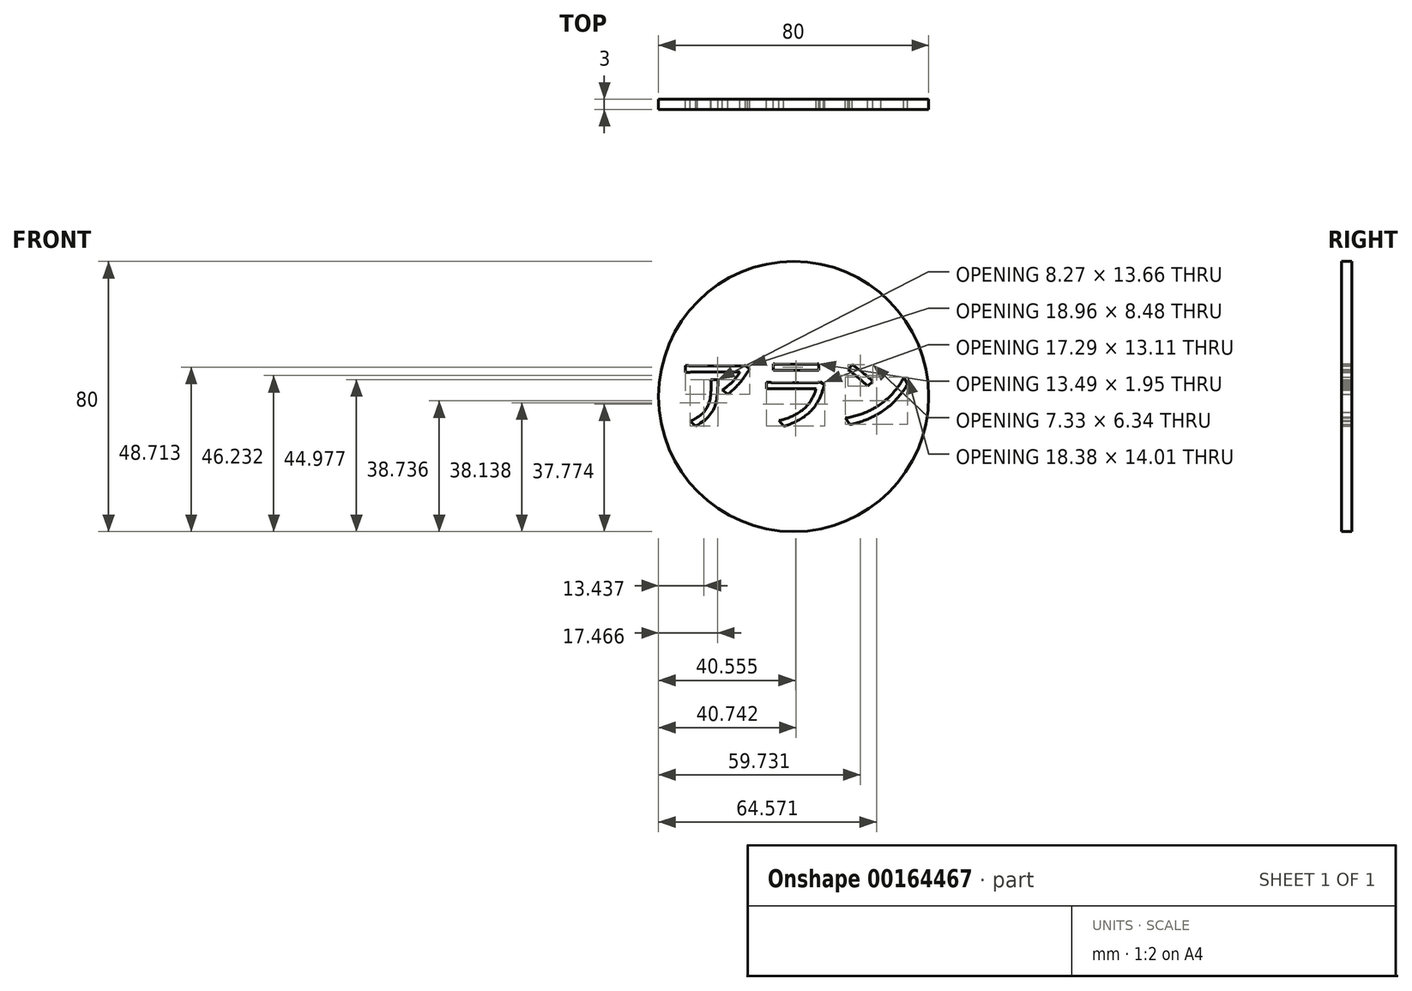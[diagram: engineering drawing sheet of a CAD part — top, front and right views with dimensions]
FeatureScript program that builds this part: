
annotation { "Feature Type Name" : "Feature", "Feature Type Description" : "" }
export const myFeature = defineFeature(function(context is Context, id is Id, definition is map)
    precondition{}
    {
        {
            var Q0;
            Q0=qCreatedBy(makeId("Front.planeOp"),FACE);
            var sketch = newSketch(context, id + "F0", { "sketchPlane" : qUnion([Q0])});
            skCircle(sketch, "E0", {"center": v(0, 0) * mm, "radius": 40 * mm});
            skText(sketch, "E1", { "text": "アラン", "fontName": "NotoSansCJKjp-Regular.otf"});
            const initialGuessF0  = {"E1": [-0.03493, -0.00782, 1, 0, 0.01692]};
            skSetInitialGuess(sketch, initialGuessF0);
            skSolve(sketch);
        }
        {
            var Q0;
            Q0=makeQuery(id+"F0.imprint","IMPRINT",FACE,{"disambiguationData":[TD([[makeQuery(id+"F0.imprint","IMPRINT",EDGE,{"derivedFrom":sQuery(id+"F0.wireOp",EDGE,"E0")}),1.0]])]});
            extrude(context, id + "F1", {"entities" : qUnion([Q0]), "depth" : 3 * mm});
        }
    });
